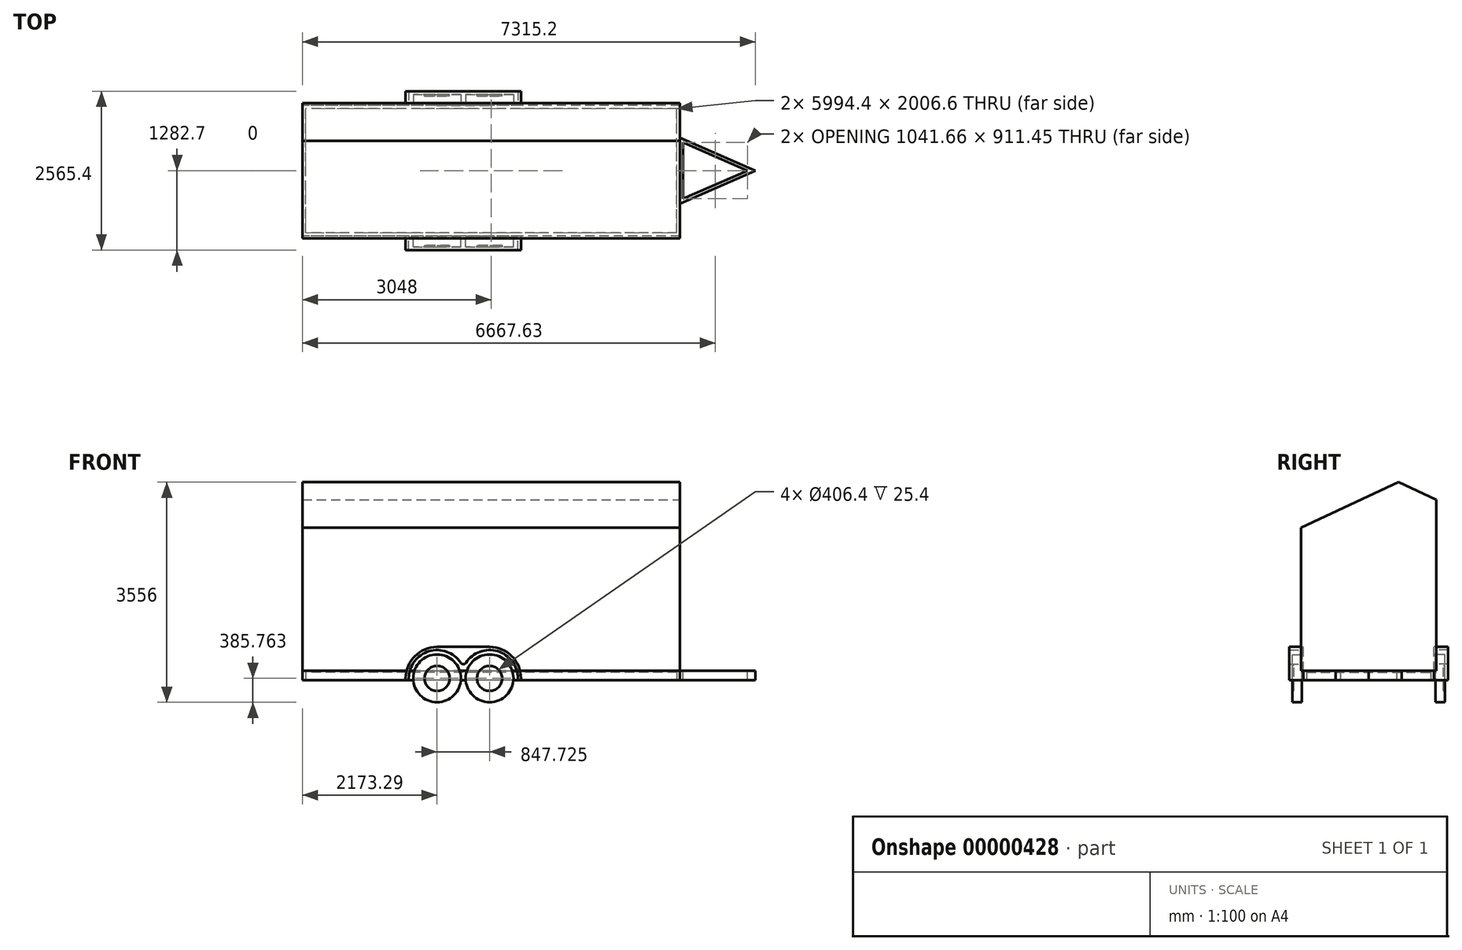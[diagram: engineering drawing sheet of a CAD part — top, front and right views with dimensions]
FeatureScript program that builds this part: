
annotation { "Feature Type Name" : "Feature", "Feature Type Description" : "" }
export const myFeature = defineFeature(function(context is Context, id is Id, definition is map)
    precondition{}
    {
        {
            var Q0;
            Q0 = qCreatedBy(makeId("Top.planeOp"), FACE);
            var sketch = newSketch(context, id + "F0", { "sketchPlane" : qUnion([Q0])});
            skLineSegment(sketch, "E0.bottom", {"start": v(3048, -1054.1) * mm, "end": v(-3048, -1054.1) * mm});
            skLineSegment(sketch, "E0.top", {"start": v(3048, 1054.1) * mm, "end": v(-3048, 1054.1) * mm});
            skLineSegment(sketch, "E0.left", {"start": v(3048, -1054.1) * mm, "end": v(3048, 1054.1) * mm});
            skLineSegment(sketch, "E0.right", {"start": v(-3048, -1054.1) * mm, "end": v(-3048, 1054.1) * mm});
            skLineSegment(sketch, "E1", {"start": v(3048, 1054.1) * mm, "end": v(-3048, -1054.1) * mm, "construction": true});
            skLineSegment(sketch, "E2.0", {"start": v(2997.2, 1003.3) * mm, "end": v(-2997.2, 1003.3) * mm});
            skLineSegment(sketch, "E2.1", {"start": v(2997.2, -1003.3) * mm, "end": v(2997.2, 1003.3) * mm});
            skLineSegment(sketch, "E2.2", {"start": v(2997.2, -1003.3) * mm, "end": v(-2997.2, -1003.3) * mm});
            skLineSegment(sketch, "E2.3", {"start": v(-2997.2, -1003.3) * mm, "end": v(-2997.2, 1003.3) * mm});
            skSolve(sketch);
        }
        {
            var Q0;
            Q0=makeQuery(id+"F0.imprint","IMPRINT",FACE,{"disambiguationData":[TD([[makeQuery(id+"F0.imprint","IMPRINT",EDGE,{"derivedFrom":sQuery(id+"F0.wireOp",EDGE,"E0.bottom")}),-1.0]])]});
            extrude(context, id + "F1", {"entities" : qUnion([Q0]), "depth" : 152.4 * mm});
        }
        {
            var Q0;
            Q0=makeQuery(id+"F1.opExtrude","CAP_FACE",FACE,{"disambiguationData":[OSD([sQuery(id+"F0.wireOp",EDGE,"E0.bottom"),sQuery(id+"F0.wireOp",EDGE,"E0.top"),sQuery(id+"F0.wireOp",EDGE,"E0.left"),sQuery(id+"F0.wireOp",EDGE,"E0.right"),sQuery(id+"F0.wireOp",EDGE,"E2.0"),sQuery(id+"F0.wireOp",EDGE,"E2.1"),sQuery(id+"F0.wireOp",EDGE,"E2.2"),sQuery(id+"F0.wireOp",EDGE,"E2.3")])],"isStart":false});
            var sketch = newSketch(context, id + "F2", { "sketchPlane" : qUnion([Q0])});
            skLineSegment(sketch, "E3", {"start": v(3048, 533.4) * mm, "end": v(4267.2, 0) * mm});
            skLineSegment(sketch, "E4", {"start": v(4267.2, 0) * mm, "end": v(3048, -533.4) * mm});
            skLineSegment(sketch, "E5", {"start": v(3048, -533.4) * mm, "end": v(3048, 533.4) * mm});
            skLineSegment(sketch, "E6", {"start": v(3048, 0) * mm, "end": v(5099.44, 0) * mm, "construction": true});
            skLineSegment(sketch, "E7.0", {"start": v(3098.8, -455.73) * mm, "end": v(3098.8, 455.73) * mm});
            skLineSegment(sketch, "E7.1", {"start": v(4140.46, 0) * mm, "end": v(3098.8, -455.73) * mm});
            skLineSegment(sketch, "E7.2", {"start": v(3098.8, 455.73) * mm, "end": v(4140.46, 0) * mm});
            skSolve(sketch);
        }
        {
            var Q0;
            Q0=makeQuery(id+"F2.imprint","IMPRINT",FACE,{"disambiguationData":[TD([[makeQuery(id+"F2.imprint","IMPRINT",EDGE,{"derivedFrom":sQuery(id+"F2.wireOp",EDGE,"E3")}),-1.0]])]});
            var Q1;
            Q1=makeQuery(id+"F1.opExtrude","CAP_FACE",FACE,{"disambiguationData":[OSD([sQuery(id+"F0.wireOp",EDGE,"E0.bottom"),sQuery(id+"F0.wireOp",EDGE,"E0.top"),sQuery(id+"F0.wireOp",EDGE,"E0.left"),sQuery(id+"F0.wireOp",EDGE,"E0.right"),sQuery(id+"F0.wireOp",EDGE,"E2.0"),sQuery(id+"F0.wireOp",EDGE,"E2.1"),sQuery(id+"F0.wireOp",EDGE,"E2.2"),sQuery(id+"F0.wireOp",EDGE,"E2.3")])],"isStart":true});
            extrude(context, id + "F3", {"entities" : qUnion([Q0]), "operationType" : NewBodyOperationType.ADD, "endBound" : BoundingType.UP_TO_SURFACE, "oppositeDirection" : true, "endBoundEntityFace" : qUnion([Q1]), "depth" : 25.4 * mm});
        }
        {
            var Q0;
            Q0=makeQuery(id+"F1.opExtrude","SWEPT_FACE",FACE,{"disambiguationData":[OSD([sQuery(id+"F0.wireOp",EDGE,"E0.bottom")])]});
            var sketch = newSketch(context, id + "F4", { "sketchPlane" : qUnion([Q0])});
            skLineSegment(sketch, "E8", {"start": v(-1382.71, 0) * mm, "end": v(-1382.71, 30.16) * mm});
            skArc(sketch, "E9", {"start": v(-874.71, 538.16) * mm, "mid": v(-1233.92, 389.37) * mm, "end": v(-1382.71, 30.16) * mm});
            skLineSegment(sketch, "E10", {"start": v(-874.71, 538.16) * mm, "end": v(-450.85, 538.16) * mm});
            skLineSegment(sketch, "E11", {"start": v(-450.85, 538.16) * mm, "end": v(-450.85, 0) * mm, "construction": true});
            skLineSegment(sketch, "E12", {"start": v(-450.85, 0) * mm, "end": v(-1382.71, 0) * mm});
            skLineSegment(sketch, "E13.0.mirrorCS.copySeg", {"start": v(-450.85, 0) * mm, "end": v(481.01, 0) * mm});
            skLineSegment(sketch, "E13.1.mirrorCS.copySeg", {"start": v(481.01, 0) * mm, "end": v(481.01, 30.16) * mm});
            skArc(sketch, "E13.2.mirrorCS.copyArc", {"start": v(-26.99, 538.16) * mm, "mid": v(332.22, 389.37) * mm, "end": v(481.01, 30.16) * mm});
            skLineSegment(sketch, "E13.3.mirrorCS.copySeg", {"start": v(-26.99, 538.16) * mm, "end": v(-450.85, 538.16) * mm});
            skPoint(sketch, "E14.0.MirrorP.copyP", {"position": v(-26.99, 538.16) * mm});
            skPoint(sketch, "E15.0.MirrorP.copyP", {"position": v(-874.71, 538.16) * mm});
            skSolve(sketch);
        }
        {
            var Q0;
            {var subQ6=sQuery(id+"F4.wireOp",EDGE,"E10");var subQ8=sQuery(id+"F4.wireOp",EDGE,"E8");Q0=qUnion([makeQuery(id+"F4.imprint","IMPRINT",FACE,{"disambiguationData":[TD([[makeQuery(id+"F4.imprint","IMPRINT",EDGE,{"derivedFrom":subQ6}),-1.0]])]}),makeQuery(id+"F4.imprint","IMPRINT",FACE,{"disambiguationData":[TD([[makeQuery(id+"F4.imprint","IMPRINT",EDGE,{"derivedFrom":subQ8}),-1.0]])]})]);}
            extrude(context, id + "F5", {"entities" : qUnion([Q0]), "operationType" : NewBodyOperationType.ADD, "depth" : 25.4 * mm});
        }
        {
            var Q0;
            Q0=makeQuery(id+"F5.opExtrude","CAP_FACE",FACE,{"disambiguationData":[OSD([sQuery(id+"F4.wireOp",EDGE,"E8"),sQuery(id+"F4.wireOp",EDGE,"E9"),sQuery(id+"F4.wireOp",EDGE,"E10"),sQuery(id+"F4.wireOp",EDGE,"E12"),sQuery(id+"F4.wireOp",EDGE,"E13.1.mirrorCS.copySeg"),sQuery(id+"F4.wireOp",EDGE,"E13.2.mirrorCS.copyArc")])],"isStart":false});
            var sketch = newSketch(context, id + "F6", { "sketchPlane" : qUnion([Q0])});
            skLineSegment(sketch, "E16.0.0", {"start": v(-874.71, 538.16) * mm, "end": v(-26.99, 538.16) * mm});
            skArc(sketch, "E16.0.1", {"start": v(-874.71, 538.16) * mm, "mid": v(-1233.92, 389.37) * mm, "end": v(-1382.71, 30.16) * mm});
            skLineSegment(sketch, "E16.0.2", {"start": v(-1382.71, 0) * mm, "end": v(-1382.71, 30.16) * mm});
            skLineSegment(sketch, "E16.0.3", {"start": v(481.01, 0) * mm, "end": v(430.21, 0) * mm});
            skLineSegment(sketch, "E16.0.4", {"start": v(481.01, 0) * mm, "end": v(481.01, 30.16) * mm});
            skArc(sketch, "E16.0.5", {"start": v(-26.99, 538.16) * mm, "mid": v(332.22, 389.37) * mm, "end": v(481.01, 30.16) * mm});
            skArc(sketch, "E17.1", {"start": v(-1331.91, 30.16) * mm, "mid": v(-1006.28, 468.02) * mm, "end": v(-493.24, 282.17) * mm});
            skArc(sketch, "E17.3", {"start": v(-408.46, 282.17) * mm, "mid": v(104.58, 468.02) * mm, "end": v(430.21, 30.16) * mm});
            skLineSegment(sketch, "E18", {"start": v(-1331.91, 30.16) * mm, "end": v(-1331.91, 0) * mm});
            skLineSegment(sketch, "E19", {"start": v(430.21, 30.16) * mm, "end": v(430.21, 0) * mm});
            skLineSegment(sketch, "E20.trimOffspring", {"start": v(-1331.91, 0) * mm, "end": v(-1382.71, 0) * mm});
            skPoint(sketch, "E21.visualSharp", {"position": v(-450.85, 201.55) * mm});
            skArc(sketch, "E21.filletArc", {"start": v(-493.24, 282.17) * mm, "mid": v(-450.85, 259.37) * mm, "end": v(-408.46, 282.17) * mm});
            skSolve(sketch);
        }
        {
            var Q0;
            Q0=makeQuery(id+"F6.imprint","IMPRINT",FACE,{"disambiguationData":[TD([[makeQuery(id+"F6.imprint","IMPRINT",EDGE,{"derivedFrom":sQuery(id+"F6.wireOp",EDGE,"E16.0.0")}),-1.0]])]});
            extrude(context, id + "F7", {"entities" : qUnion([Q0]), "operationType" : NewBodyOperationType.ADD, "depth" : 203.2 * mm});
        }
        {
            var Q0;
            Q0=makeQuery(id+"F5.opExtrude","CAP_FACE",FACE,{"disambiguationData":[OSD([sQuery(id+"F4.wireOp",EDGE,"E8"),sQuery(id+"F4.wireOp",EDGE,"E9"),sQuery(id+"F4.wireOp",EDGE,"E10"),sQuery(id+"F4.wireOp",EDGE,"E12"),sQuery(id+"F4.wireOp",EDGE,"E13.1.mirrorCS.copySeg"),sQuery(id+"F4.wireOp",EDGE,"E13.2.mirrorCS.copyArc")])],"isStart":false});
            var sketch = newSketch(context, id + "F8", { "sketchPlane" : qUnion([Q0])});
            skCircle(sketch, "E22", {"center": v(-874.71, 30.16) * mm, "radius": 385.76 * mm});
            skCircle(sketch, "E23", {"center": v(-26.99, 30.16) * mm, "radius": 385.76 * mm});
            skSolve(sketch);
        }
        {
            var Q0;
            {var subQ0=makeQuery(id+"F5.opExtrude","CAP_EDGE",EDGE,{"disambiguationData":[OSD([sQuery(id+"F4.wireOp",EDGE,"E12")])],"isStart":false});var subQ1=sQuery(id+"F8.wireOp",EDGE,"E22");var subQ3=makeQuery(id+"F8.imprint","INTERSECT",VERTEX,{"disambiguationData":[OD(0.0)],"derivedFrom":[subQ0,subQ1]});var subQ5=sQuery(id+"F8.wireOp",EDGE,"E23");var subQ7=makeQuery(id+"F8.imprint","INTERSECT",VERTEX,{"disambiguationData":[OD(0.0)],"derivedFrom":[subQ0,subQ5]});Q0=qUnion([makeQuery(id+"F8.imprint","IMPRINT",FACE,{"disambiguationData":[TD([[makeQuery(id+"F8.imprint","IMPRINT",EDGE,{"disambiguationData":[TD([[subQ3,-1.0]])],"derivedFrom":subQ1}),1.0]])]}),makeQuery(id+"F8.imprint","IMPRINT",FACE,{"disambiguationData":[TD([[makeQuery(id+"F8.imprint","IMPRINT",EDGE,{"disambiguationData":[TD([[subQ7,1.0]])],"derivedFrom":subQ5}),1.0]])]}),makeQuery(id+"F8.imprint","IMPRINT",FACE,{"disambiguationData":[TD([[makeQuery(id+"F8.imprint","IMPRINT",EDGE,{"disambiguationData":[TD([[subQ3,1.0]])],"derivedFrom":subQ1}),1.0]])]}),makeQuery(id+"F8.imprint","IMPRINT",FACE,{"disambiguationData":[TD([[makeQuery(id+"F8.imprint","IMPRINT",EDGE,{"disambiguationData":[TD([[subQ7,-1.0]])],"derivedFrom":subQ5}),1.0]])]})]);}
            extrude(context, id + "F9", {"entities" : qUnion([Q0]), "depth" : 152.4 * mm});
        }
        {
            var Q0;
            Q0=makeQuery(id+"F9.opExtrude","CAP_FACE",FACE,{"disambiguationData":[OSD([sQuery(id+"F8.wireOp",EDGE,"E22")])],"isStart":false});
            var sketch = newSketch(context, id + "F10", { "sketchPlane" : qUnion([Q0])});
            skCircle(sketch, "E24", {"center": v(-874.71, 30.16) * mm, "radius": 203.2 * mm});
            skCircle(sketch, "E25", {"center": v(-26.99, 30.16) * mm, "radius": 203.2 * mm});
            skSolve(sketch);
        }
        {
            var Q0;
            {Q0=qUnion([makeQuery(id+"F10.imprint","IMPRINT",FACE,{"disambiguationData":[TD([[makeQuery(id+"F10.imprint","IMPRINT",EDGE,{"derivedFrom":sQuery(id+"F10.wireOp",EDGE,"E25")}),1.0]])]}),makeQuery(id+"F10.imprint","IMPRINT",FACE,{"disambiguationData":[TD([[makeQuery(id+"F10.imprint","IMPRINT",EDGE,{"derivedFrom":sQuery(id+"F10.wireOp",EDGE,"E24")}),1.0]])]})]);}
            extrude(context, id + "F11", {"entities" : qUnion([Q0]), "operationType" : NewBodyOperationType.REMOVE, "oppositeDirection" : true, "depth" : 25.4 * mm});
        }
        {
            var Q0;
            Q0=makeQuery(id+"F3.boolean.opBoolean","MERGE",FACE,{"derivedFrom":[makeQuery(id+"F1.opExtrude","CAP_FACE",FACE,{"disambiguationData":[OSD([sQuery(id+"F0.wireOp",EDGE,"E0.bottom"),sQuery(id+"F0.wireOp",EDGE,"E0.top"),sQuery(id+"F0.wireOp",EDGE,"E0.left"),sQuery(id+"F0.wireOp",EDGE,"E0.right"),sQuery(id+"F0.wireOp",EDGE,"E2.0"),sQuery(id+"F0.wireOp",EDGE,"E2.1"),sQuery(id+"F0.wireOp",EDGE,"E2.2"),sQuery(id+"F0.wireOp",EDGE,"E2.3")])],"isStart":false}),makeQuery(id+"F3.opExtrude","CAP_FACE",FACE,{"disambiguationData":[OSD([sQuery(id+"F2.wireOp",EDGE,"E3"),sQuery(id+"F2.wireOp",EDGE,"E4"),sQuery(id+"F2.wireOp",EDGE,"E5"),sQuery(id+"F2.wireOp",EDGE,"E7.0"),sQuery(id+"F2.wireOp",EDGE,"E7.1"),sQuery(id+"F2.wireOp",EDGE,"E7.2")])],"isStart":true})]});
            var sketch = newSketch(context, id + "F12", { "sketchPlane" : qUnion([Q0])});
            skLineSegment(sketch, "E26.0", {"start": v(2997.2, 1003.3) * mm, "end": v(-2997.2, 1003.3) * mm});
            skLineSegment(sketch, "E26.1", {"start": v(-2997.2, -1003.3) * mm, "end": v(-2997.2, 1003.3) * mm});
            skLineSegment(sketch, "E26.2", {"start": v(2997.2, -1003.3) * mm, "end": v(2997.2, 1003.3) * mm});
            skLineSegment(sketch, "E26.3", {"start": v(2997.2, -1003.3) * mm, "end": v(-2997.2, -1003.3) * mm});
            skSolve(sketch);
        }
        {
            var Q0;
            Q0=makeQuery(id+"F12.imprint","IMPRINT",FACE,{"disambiguationData":[TD([[makeQuery(id+"F12.imprint","IMPRINT",EDGE,{"derivedFrom":sQuery(id+"F12.wireOp",EDGE,"E26.0")}),1.0]])]});
            extrude(context, id + "F13", {"entities" : qUnion([Q0]), "oppositeDirection" : true, "depth" : 25.4 * mm});
        }
        {
            var Q0;
            Q0=makeQuery(id+"F1.opExtrude","SWEPT_BODY",BODY,{"disambiguationData":[OSD([sQuery(id+"F0.wireOp",EDGE,"E0.bottom"),sQuery(id+"F0.wireOp",EDGE,"E0.top"),sQuery(id+"F0.wireOp",EDGE,"E0.left"),sQuery(id+"F0.wireOp",EDGE,"E0.right"),sQuery(id+"F0.wireOp",EDGE,"E2.0"),sQuery(id+"F0.wireOp",EDGE,"E2.1"),sQuery(id+"F0.wireOp",EDGE,"E2.2"),sQuery(id+"F0.wireOp",EDGE,"E2.3")])]});
            var Q1;
            Q1 = qCreatedBy(makeId("Front.planeOp"), FACE);
            mirror(context, id + "F14", {"entities" : qUnion([Q0]), "mirrorPlane" : qUnion([Q1])});
        }
        {
            var Q0;
            Q0=makeQuery(id+"F9.opExtrude","SWEPT_BODY",BODY,{"disambiguationData":[OSD([sQuery(id+"F8.wireOp",EDGE,"E23")])]});
            var Q1;
            Q1=makeQuery(id+"F9.opExtrude","SWEPT_BODY",BODY,{"disambiguationData":[OSD([sQuery(id+"F8.wireOp",EDGE,"E22")])]});
            var Q2;
            Q2 = qCreatedBy(makeId("Front.planeOp"), FACE);
            mirror(context, id + "F15", {"entities" : qUnion([Q0, Q1]), "mirrorPlane" : qUnion([Q2])});
        }
        {
            var Q0;
            Q0=makeQuery(id+"F14.opPattern","COPY",FACE,{"derivedFrom":makeQuery(id+"F3.boolean.opBoolean","MERGE",FACE,{"derivedFrom":[makeQuery(id+"F1.opExtrude","CAP_FACE",FACE,{"disambiguationData":[OSD([sQuery(id+"F0.wireOp",EDGE,"E0.bottom"),sQuery(id+"F0.wireOp",EDGE,"E0.top"),sQuery(id+"F0.wireOp",EDGE,"E0.left"),sQuery(id+"F0.wireOp",EDGE,"E0.right"),sQuery(id+"F0.wireOp",EDGE,"E2.0"),sQuery(id+"F0.wireOp",EDGE,"E2.1"),sQuery(id+"F0.wireOp",EDGE,"E2.2"),sQuery(id+"F0.wireOp",EDGE,"E2.3")])],"isStart":false}),makeQuery(id+"F3.opExtrude","CAP_FACE",FACE,{"disambiguationData":[OSD([sQuery(id+"F2.wireOp",EDGE,"E3"),sQuery(id+"F2.wireOp",EDGE,"E4"),sQuery(id+"F2.wireOp",EDGE,"E5"),sQuery(id+"F2.wireOp",EDGE,"E7.0"),sQuery(id+"F2.wireOp",EDGE,"E7.1"),sQuery(id+"F2.wireOp",EDGE,"E7.2")])],"isStart":true})]}),"instanceName":"1"});
            var sketch = newSketch(context, id + "F16", { "sketchPlane" : qUnion([Q0])});
            skLineSegment(sketch, "E27.bottom", {"start": v(-3048, 1092.2) * mm, "end": v(3048, 1092.2) * mm});
            skLineSegment(sketch, "E27.top", {"start": v(-3048, -1092.2) * mm, "end": v(3048, -1092.2) * mm});
            skLineSegment(sketch, "E27.left", {"start": v(-3048, 1092.2) * mm, "end": v(-3048, -1092.2) * mm});
            skLineSegment(sketch, "E27.right", {"start": v(3048, 1092.2) * mm, "end": v(3048, -1092.2) * mm});
            skLineSegment(sketch, "E28", {"start": v(0, 0) * mm, "end": v(3048, 0) * mm, "construction": true});
            skSolve(sketch);
        }
        {
            var Q0;
            {var subQ16=sQuery(id+"F0.wireOp",EDGE,"E2.0");var subQ29=sQuery(id+"F16.wireOp",EDGE,"E27.bottom");var subQ45=sQuery(id+"F16.wireOp",EDGE,"E27.top");var subQ51=makeQuery(id+"F16.imprint","IMPRINT",EDGE,{"derivedFrom":makeQuery(id+"F14.opPattern","COPY",EDGE,{"derivedFrom":makeQuery(id+"F1.opExtrude","CAP_EDGE",EDGE,{"disambiguationData":[OSD([subQ16])],"isStart":false}),"instanceName":"1"})});Q0=qUnion([makeQuery(id+"F16.imprint","IMPRINT",FACE,{"disambiguationData":[TD([[makeQuery(id+"F16.imprint","IMPRINT",EDGE,{"derivedFrom":subQ29}),-1.0]])]}),makeQuery(id+"F16.imprint","IMPRINT",FACE,{"disambiguationData":[TD([[makeQuery(id+"F16.imprint","IMPRINT",EDGE,{"derivedFrom":subQ45}),1.0]])]}),makeQuery(id+"F16.imprint","IMPRINT",FACE,{"disambiguationData":[TD([[subQ51,-1.0]])]}),makeQuery(id+"F16.imprint","IMPRINT",FACE,{"disambiguationData":[TD([[subQ51,1.0]])]})]);}
            extrude(context, id + "F17", {"entities" : qUnion([Q0]), "depth" : 3048 * mm});
        }
        {
            var Q0;
            Q0=makeQuery(id+"F17.opExtrude","SWEPT_FACE",FACE,{"disambiguationData":[OSD([sQuery(id+"F16.wireOp",EDGE,"E27.right")])]});
            var sketch = newSketch(context, id + "F18", { "sketchPlane" : qUnion([Q0])});
            skLineSegment(sketch, "E29", {"start": v(-1092.2, 2466.06) * mm, "end": v(482.6, 3200.4) * mm});
            skLineSegment(sketch, "E30", {"start": v(482.6, 3200.4) * mm, "end": v(1092.2, 2916.14) * mm});
            skLineSegment(sketch, "E31", {"start": v(1092.2, 2916.14) * mm, "end": v(1092.2, 3200.4) * mm});
            skLineSegment(sketch, "E32", {"start": v(1092.2, 3200.4) * mm, "end": v(-1092.2, 3200.4) * mm});
            skLineSegment(sketch, "E33", {"start": v(-1092.2, 3200.4) * mm, "end": v(-1092.2, 2466.06) * mm});
            skSolve(sketch);
        }
        {
            var Q0;
            {var subQ2=sQuery(id+"F18.wireOp",EDGE,"E29");var subQ3=sQuery(id+"F18.wireOp",EDGE,"E30");Q0=qUnion([makeQuery(id+"F18.imprint","IMPRINT",FACE,{"disambiguationData":[TD([[makeQuery(id+"F18.imprint","IMPRINT",EDGE,{"derivedFrom":subQ2}),1.0]])]}),makeQuery(id+"F18.imprint","IMPRINT",FACE,{"disambiguationData":[TD([[makeQuery(id+"F18.imprint","IMPRINT",EDGE,{"derivedFrom":subQ3}),1.0]])]})]);}
            extrude(context, id + "F19", {"entities" : qUnion([Q0]), "operationType" : NewBodyOperationType.REMOVE, "endBound" : BoundingType.UP_TO_NEXT, "oppositeDirection" : true, "depth" : 25.4 * mm});
        }
    });
